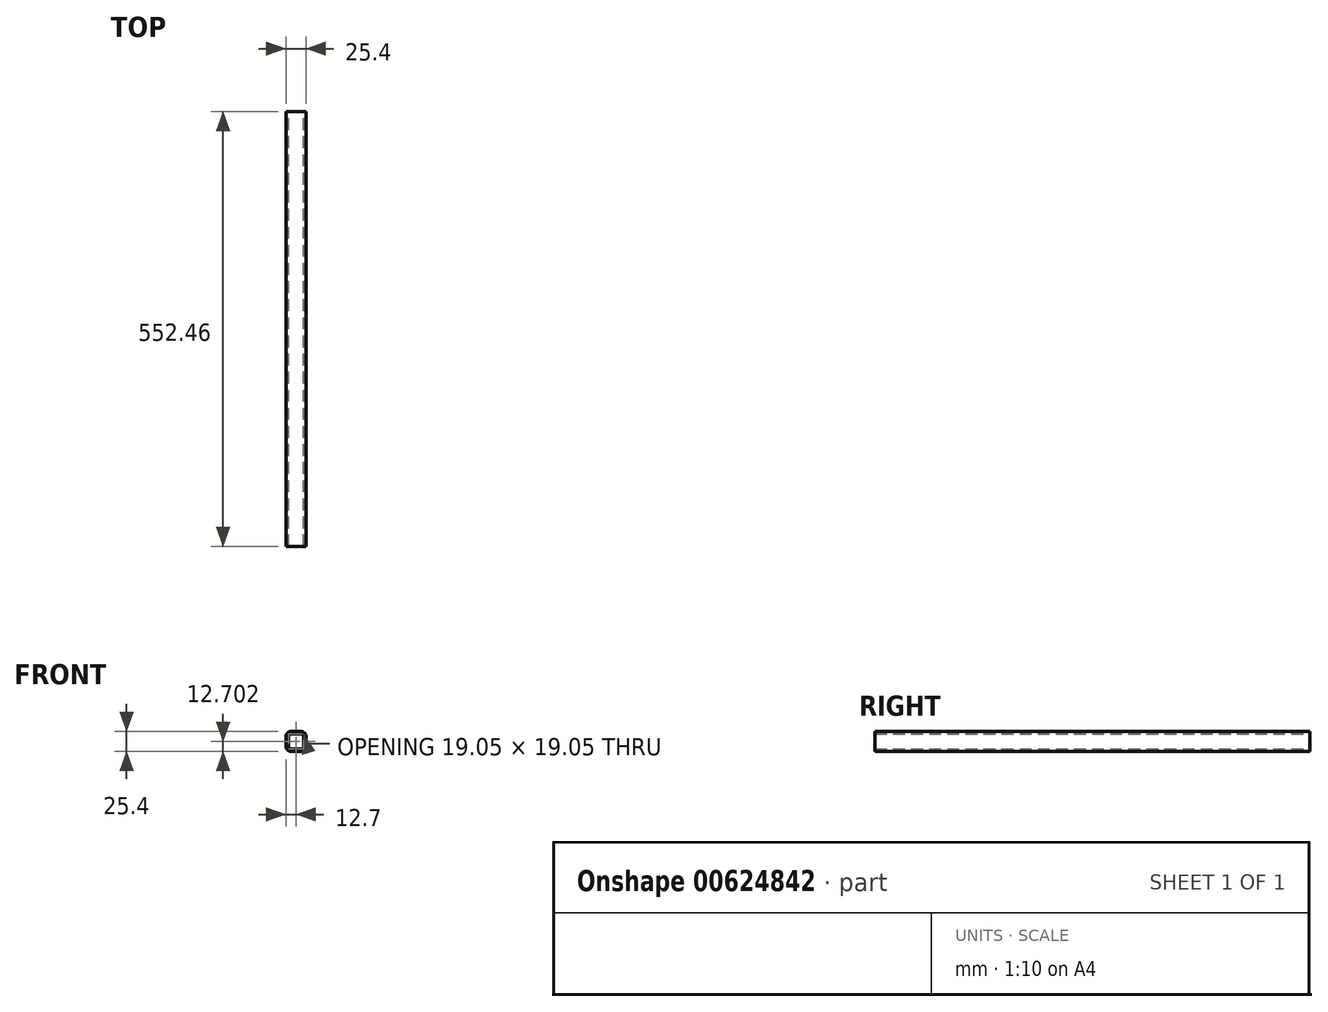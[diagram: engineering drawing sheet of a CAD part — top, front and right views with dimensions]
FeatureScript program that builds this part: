
annotation { "Feature Type Name" : "Feature", "Feature Type Description" : "" }
export const myFeature = defineFeature(function(context is Context, id is Id, definition is map)
    precondition{}
    {
        {
            var Q0;
            Q0=qCreatedBy(makeId("Front.planeOp"),FACE);
            var sketch = newSketch(context, id + "F0", { "sketchPlane" : qUnion([Q0])});
            skLineSegment(sketch, "E0.bottom", {"start": v(-6.35, 13.31) * mm, "end": v(6.35, 13.31) * mm});
            skLineSegment(sketch, "E0.top", {"start": v(-6.35, -12.09) * mm, "end": v(6.35, -12.09) * mm});
            skLineSegment(sketch, "E0.left", {"start": v(-12.7, 6.96) * mm, "end": v(-12.7, -5.74) * mm});
            skLineSegment(sketch, "E0.right", {"start": v(12.7, 6.96) * mm, "end": v(12.7, -5.74) * mm});
            skPoint(sketch, "E0.middle", {"position": v(0, 0.61) * mm});
            skPoint(sketch, "E1.visualSharp", {"position": v(-12.7, 13.31) * mm});
            skArc(sketch, "E1.filletArc", {"start": v(-11.77, 10.28) * mm, "mid": v(-12.46, 8.68) * mm, "end": v(-12.7, 6.96) * mm});
            skPoint(sketch, "E2.visualSharp", {"position": v(-6.35, 13.31) * mm});
            skArc(sketch, "E2.filletArc", {"start": v(-6.35, 13.31) * mm, "mid": v(-9.45, 12.5) * mm, "end": v(-11.77, 10.28) * mm});
            skPoint(sketch, "E3.visualSharp", {"position": v(12.7, 13.31) * mm});
            skArc(sketch, "E3.filletArc", {"start": v(12.7, 6.96) * mm, "mid": v(10.84, 11.45) * mm, "end": v(6.35, 13.31) * mm});
            skPoint(sketch, "E4.visualSharp", {"position": v(12.7, -12.09) * mm});
            skArc(sketch, "E4.filletArc", {"start": v(6.35, -12.09) * mm, "mid": v(10.84, -10.23) * mm, "end": v(12.7, -5.74) * mm});
            skPoint(sketch, "E5.visualSharp", {"position": v(-12.7, -12.09) * mm});
            skArc(sketch, "E5.filletArc", {"start": v(-12.7, -5.74) * mm, "mid": v(-10.84, -10.23) * mm, "end": v(-6.35, -12.09) * mm});
            skLineSegment(sketch, "E6.0", {"start": v(-9.52, 6.96) * mm, "end": v(-9.53, -5.74) * mm});
            skArc(sketch, "E6.1", {"start": v(-9.53, -5.74) * mm, "mid": v(-8.6, -7.98) * mm, "end": v(-6.35, -8.91) * mm});
            skLineSegment(sketch, "E6.2", {"start": v(-6.35, -8.91) * mm, "end": v(6.35, -8.91) * mm});
            skArc(sketch, "E6.3", {"start": v(6.35, -8.91) * mm, "mid": v(8.6, -7.98) * mm, "end": v(9.52, -5.74) * mm});
            skArc(sketch, "E6.4", {"start": v(-6.35, 10.14) * mm, "mid": v(-8.6, 9.2) * mm, "end": v(-9.52, 6.96) * mm});
            skLineSegment(sketch, "E6.5", {"start": v(-6.35, 10.14) * mm, "end": v(6.35, 10.14) * mm});
            skArc(sketch, "E6.6", {"start": v(9.53, 6.96) * mm, "mid": v(8.6, 9.2) * mm, "end": v(6.35, 10.14) * mm});
            skLineSegment(sketch, "E6.7", {"start": v(9.53, 6.96) * mm, "end": v(9.52, -5.74) * mm});
            skSolve(sketch);
        }
        {
            var Q0;
            Q0=qSketchRegion(id+"F0",true);
            extrude(context, id + "F1", {"entities" : qUnion([Q0]), "endBound" : BoundingType.SYMMETRIC, "depth" : 552.45 * mm, "offsetDistance" : 25.4 * mm});
        }
    });
